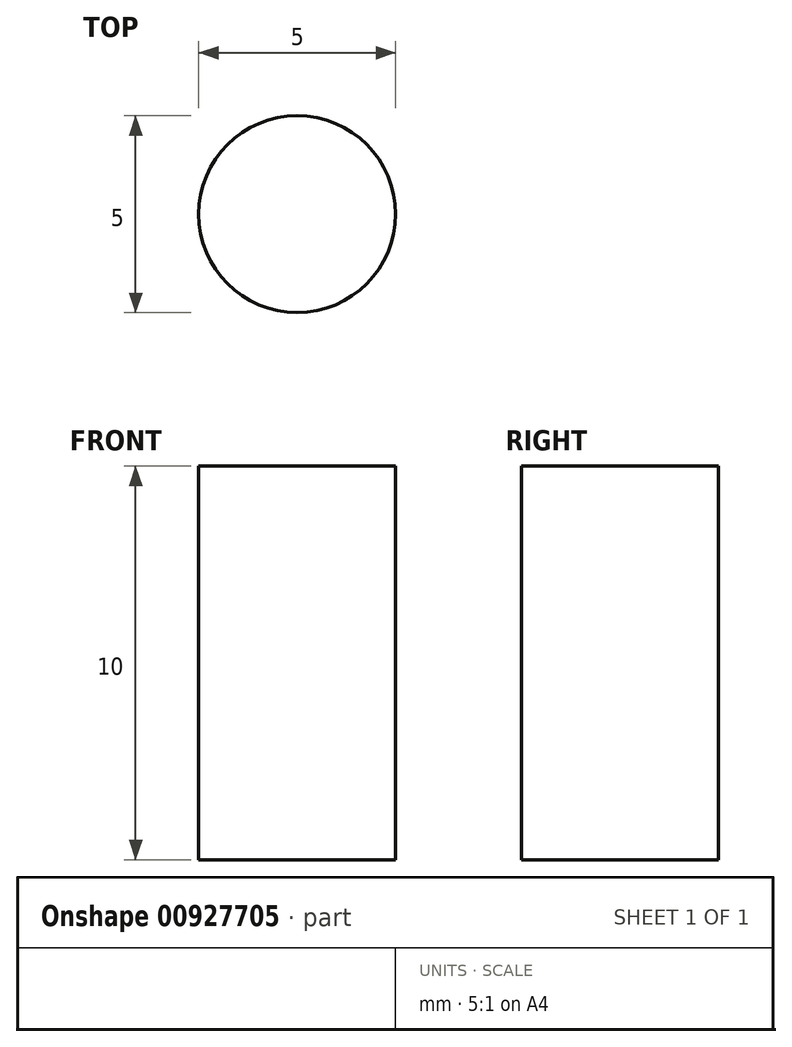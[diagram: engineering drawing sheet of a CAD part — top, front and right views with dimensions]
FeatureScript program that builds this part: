
annotation { "Feature Type Name" : "Feature", "Feature Type Description" : "" }
export const myFeature = defineFeature(function(context is Context, id is Id, definition is map)
    precondition{}
    {
        {
            var Q0;
            Q0=qCreatedBy(makeId("Top.planeOp"),FACE);
            var sketch = newSketch(context, id + "F0", { "sketchPlane" : qUnion([Q0])});
            skCircle(sketch, "E0", {"center": v(0, 0) * mm, "radius": 2.5 * mm});
            skSolve(sketch);
        }
        {
            var Q0;
            Q0 = qSketchRegion(id + "F0", true);
            extrude(context, id + "F1", {"entities" : qUnion([Q0]), "depth" : 10 * mm, "offsetDistance" : 25 * mm});
        }
    });
